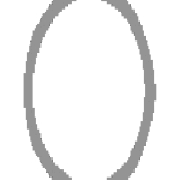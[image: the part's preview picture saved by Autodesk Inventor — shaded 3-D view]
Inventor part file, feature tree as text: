
AUTODESK INVENTOR PART (.ipt)
format: ipt  version: 2021 (Build 250183000, 183)  size: 109,568 bytes
history: native  units: in
note: dims shown in document units (in); Inventor stores cm internally (conversion verified against a paired STEP export)
features: other x4, sketch x3, plane x1
ambient origin geometry x8: Origin, YZ Plane, XZ Plane, XY Plane, X Axis, Y Axis, Z Axis, Center Point
bodies: Solid1 (feature_tree), Body (feature_tree)
feature tree (8):
  other  "Driven Length"
  other  "Frame Generator"
  other  "Start Plane"
  other  "End Plane"
  sketch  "Sketch"  dims[d2=21.5in d4=-0.0in d5=21.5in d6=0.12in d7=0.0in d8=90.0deg d9=21.5in]
  sketch  "Sketch2"  dims[d0=1.0in]
  plane  "Work Plane3"
  sketch  "Sketch3"  dims[d1=0.065in]
